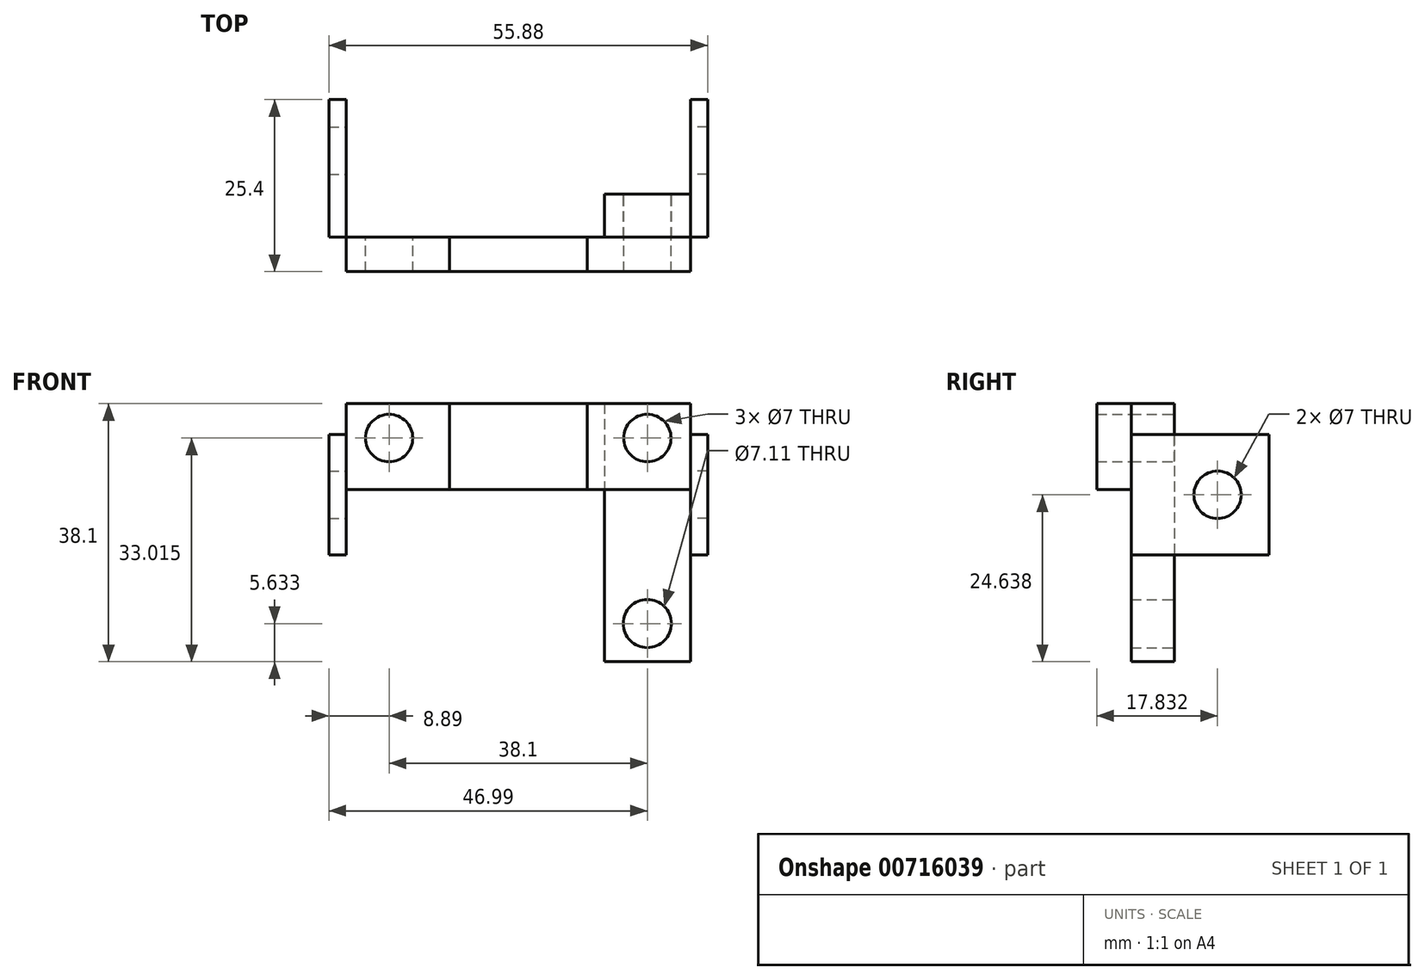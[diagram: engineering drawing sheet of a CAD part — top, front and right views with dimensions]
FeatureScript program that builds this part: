
annotation { "Feature Type Name" : "Feature", "Feature Type Description" : "" }
export const myFeature = defineFeature(function(context is Context, id is Id, definition is map)
    precondition{}
    {
        {
            var Q0;
            Q0=qCreatedBy(makeId("Front.planeOp"),FACE);
            var sketch = newSketch(context, id + "F0", { "sketchPlane" : qUnion([Q0])});
            skLineSegment(sketch, "E0.bottom", {"start": v(12.7, 38.1) * mm, "end": v(25.4, 38.1) * mm});
            skLineSegment(sketch, "E0.top", {"start": v(12.7, 0) * mm, "end": v(25.4, 0) * mm});
            skLineSegment(sketch, "E0.left", {"start": v(12.7, 38.1) * mm, "end": v(12.7, 0) * mm});
            skLineSegment(sketch, "E0.right", {"start": v(25.4, 38.1) * mm, "end": v(25.4, 0) * mm});
            skCircle(sketch, "E1", {"center": v(19.05, 33.01) * mm, "radius": 3.5 * mm});
            skPoint(sketch, "E1.centerSnap0", {"position": v(19.05, 38.1) * mm});
            skLineSegment(sketch, "E2", {"start": v(19.05, 0) * mm, "end": v(19.05, 38.1) * mm, "construction": true});
            skCircle(sketch, "E3", {"center": v(19.05, 5.63) * mm, "radius": 3.56 * mm});
            skSolve(sketch);
        }
        {
            var Q0;
            Q0=qSketchRegion(id+"F0",true);
            extrude(context, id + "F1", {"entities" : qUnion([Q0]), "depth" : 6.35 * mm, "offsetDistance" : 25.4 * mm});
        }
        {
            var Q0;
            Q0=makeQuery(id+"F1.opExtrude","CAP_FACE",FACE,{"disambiguationData":[OSD([sQuery(id+"F0.wireOp",EDGE,"E0.bottom"),sQuery(id+"F0.wireOp",EDGE,"E0.top"),sQuery(id+"F0.wireOp",EDGE,"E0.left"),sQuery(id+"F0.wireOp",EDGE,"E0.right"),sQuery(id+"F0.wireOp",EDGE,"E1")])],"isStart":false});
            var sketch = newSketch(context, id + "F2", { "sketchPlane" : qUnion([Q0])});
            skCircle(sketch, "E4", {"center": v(19.05, 33.01) * mm, "radius": 3.5 * mm});
            skLineSegment(sketch, "E5", {"start": v(25.4, 19.05) * mm, "end": v(25.4, -4.34) * mm, "construction": true});
            skLineSegment(sketch, "E6", {"start": v(25.4, -4.34) * mm, "end": v(-9.24, -4.34) * mm, "construction": true});
            skLineSegment(sketch, "E7", {"start": v(-10.16, 25.4) * mm, "end": v(25.4, 25.4) * mm, "construction": true});
            skLineSegment(sketch, "E8.bottom", {"start": v(25.4, 25.4) * mm, "end": v(-10.16, 25.4) * mm});
            skLineSegment(sketch, "E8.top", {"start": v(25.4, 38.1) * mm, "end": v(-10.16, 38.1) * mm});
            skLineSegment(sketch, "E8.left", {"start": v(25.4, 25.4) * mm, "end": v(25.4, 38.1) * mm});
            skLineSegment(sketch, "E8.right", {"start": v(-10.16, 25.4) * mm, "end": v(-10.16, 38.1) * mm});
            skSolve(sketch);
        }
        {
            var Q0;
            Q0=qSketchRegion(id+"F2",true);
            extrude(context, id + "F3", {"entities" : qUnion([Q0]), "depth" : 5.08 * mm, "offsetDistance" : 25.4 * mm});
        }
        {
            var Q0;
            Q0=makeQuery(id+"F3.opExtrude","SWEPT_BODY",BODY,{"disambiguationData":[OSD([sQuery(id+"F2.wireOp",EDGE,"FvGwd2aR-DdLF-ptD5-V0zB-aNURW71SK1EE.bottom"),sQuery(id+"F2.wireOp",EDGE,"FvGwd2aR-DdLF-ptD5-V0zB-aNURW71SK1EE.top"),sQuery(id+"F2.wireOp",EDGE,"FvGwd2aR-DdLF-ptD5-V0zB-aNURW71SK1EE.left"),sQuery(id+"F2.wireOp",EDGE,"FvGwd2aR-DdLF-ptD5-V0zB-aNURW71SK1EE.right"),sQuery(id+"F2.wireOp",EDGE,"E4")])]});
            var Q1;
            Q1=qCreatedBy(makeId("Right.planeOp"),FACE);
            mirror(context, id + "F4", {"entities" : qUnion([Q0]), "mirrorPlane" : qUnion([Q1])});
        }
        {
            var Q0;
            Q0=makeQuery(id+"F1.opExtrude","SWEPT_BODY",BODY,{"disambiguationData":[OSD([sQuery(id+"F0.wireOp",EDGE,"E0.bottom"),sQuery(id+"F0.wireOp",EDGE,"E0.top"),sQuery(id+"F0.wireOp",EDGE,"E0.left"),sQuery(id+"F0.wireOp",EDGE,"E0.right"),sQuery(id+"F0.wireOp",EDGE,"E1")])]});
            var Q1;
            Q1=qCreatedBy(makeId("Right.planeOp"),FACE);
            mirror(context, id + "F5", {"entities" : qUnion([Q0]), "mirrorPlane" : qUnion([Q1])});
        }
        {
            var Q0;
            Q0=makeQuery(id+"F1.opExtrude","SWEPT_FACE",FACE,{"disambiguationData":[OSD([sQuery(id+"F0.wireOp",EDGE,"E0.right")])]});
            var sketch = newSketch(context, id + "F6", { "sketchPlane" : qUnion([Q0])});
            skLineSegment(sketch, "E9", {"start": v(-3.3, 24.64) * mm, "end": v(3.05, 24.64) * mm, "construction": true});
            skLineSegment(sketch, "E10.bottom", {"start": v(-6.35, 15.75) * mm, "end": v(13.97, 15.75) * mm});
            skLineSegment(sketch, "E10.top", {"start": v(-6.35, 33.53) * mm, "end": v(13.97, 33.53) * mm});
            skLineSegment(sketch, "E10.left", {"start": v(-6.35, 15.75) * mm, "end": v(-6.35, 33.53) * mm});
            skLineSegment(sketch, "E10.right", {"start": v(13.97, 15.75) * mm, "end": v(13.97, 33.53) * mm});
            skCircle(sketch, "E11", {"center": v(6.4, 24.64) * mm, "radius": 3.5 * mm});
            skSolve(sketch);
        }
        {
            var Q0;
            Q0=qSketchRegion(id+"F6",true);
            extrude(context, id + "F7", {"entities" : qUnion([Q0]), "depth" : 2.54 * mm, "offsetDistance" : 25.4 * mm});
        }
        {
            var Q0;
            Q0=makeQuery(id+"F7.opExtrude","SWEPT_BODY",BODY,{"disambiguationData":[OSD([sQuery(id+"F6.wireOp",EDGE,"E10.bottom"),sQuery(id+"F6.wireOp",EDGE,"E10.top"),sQuery(id+"F6.wireOp",EDGE,"E10.left"),sQuery(id+"F6.wireOp",EDGE,"E10.right")])]});
            var Q1;
            Q1=qCreatedBy(makeId("Right.planeOp"),FACE);
            mirror(context, id + "F8", {"entities" : qUnion([Q0]), "mirrorPlane" : qUnion([Q1])});
        }
        {
            var Q0;
            Q0=makeQuery(id+"F5.opPattern","COPY",BODY,{"derivedFrom":makeQuery(id+"F1.opExtrude","SWEPT_BODY",BODY,{"disambiguationData":[OSD([sQuery(id+"F0.wireOp",EDGE,"E0.bottom"),sQuery(id+"F0.wireOp",EDGE,"E0.top"),sQuery(id+"F0.wireOp",EDGE,"E0.left"),sQuery(id+"F0.wireOp",EDGE,"E0.right"),sQuery(id+"F0.wireOp",EDGE,"E1")])]}),"instanceName":"1"});
            deleteBodies(context, id + "F9", {"entities" : qUnion([Q0])});
        }
    });
